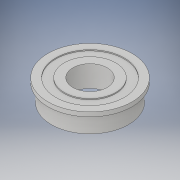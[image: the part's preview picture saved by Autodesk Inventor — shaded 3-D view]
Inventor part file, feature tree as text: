
AUTODESK INVENTOR PART (.ipt)
format: ipt  version: 2019 (Build 230136000, 136)  size: 137,728 bytes
history: native  units: in
note: dims shown in document units (in); Inventor stores cm internally (conversion verified against a paired STEP export)
features: revolve x1
ambient origin geometry x8: Origin, YZ Plane, XZ Plane, XY Plane, X Axis, Y Axis, Z Axis, Center Point
bodies: Solid1 (feature_tree)
feature tree (1):
  revolve  "Revolve1"  [1 undecoded]
note: 1 required parameter value undecoded (feature->parameter linkage not recoverable at this tier; creation-order binding heuristic only, values carry confidence <= 0.55)
